# Revit family: Haworth_Planes_CollaborativeTable_Pebble
name_source: partatom
category: Furniture Systems
revit_build: Autodesk Revit 2018 (Build: 20170223_1515(x64)
units: mm (PartAtom-declared; Revit-internal decimal feet)

## family parameters
Always vertical = Yes
Cut with Voids When Loaded = No
OmniClass Number = 23.40.70.14.64.21
OmniClass Title = Systems Furniture
Part Type = Normal
Room Calculation Point = No
Round Connector Dimension = Use Diameter
Shared = No
Work Plane-Based = No

## types (1)
- 96w 36d
    Actual Depth = 36"
    Actual Height = 29"
    Actual Width = 96"
    Assembly Code = E2020200
    Caster Finish = Haworth _ Paint _ Metallic Champagne
    Casters = Yes
    Custom 30 = Yes
    Custom 36 = No
    Custom Size = No
    Cutout = Yes
    Cutout Depth = 4"
    Cutout Width = 8"
    Depth = 36"
    Description = Haworth - Planes Collaborative Table - Pebble
    Flip Top = Yes
    Flip Top Depth = 4 7/16"
    Flip Top Finish = Haworth _ Paint _ Metallic Champagne
    Flip Top Width = 8 5/16"
    Glides = No
    Leg Height = 27 13/16"
    Manufacturer = Haworth
    Max. Depth = 36"
    Max. Width = 96"
    Min. Depth = 30"
    Min. Width = 60"
    Min/Max Depth = 30 or 36 in.
    Min/Max Width = 60-96 in. @ 6 in. increments
    Model = TARP
    Opening Single = Yes
    Opening Single Wide = No
    Revision Number = 6
    Size = Verify Final Dim. w/ Haworth
    Stretcher Width = 66"
    Support Spacing - From Edge = 15"
    Sustainability Info = https://www.haworth.com
    Table Thickness = 1 3/16"
    URL = www.haworth.com
    URL - Product = http://www.haworth.com
    Warranty = http://www.haworth.com
    Width = 96"

## geometry (parser evidence)
native form markers: Sweep x9
no freeform markers — native parametric forms only
